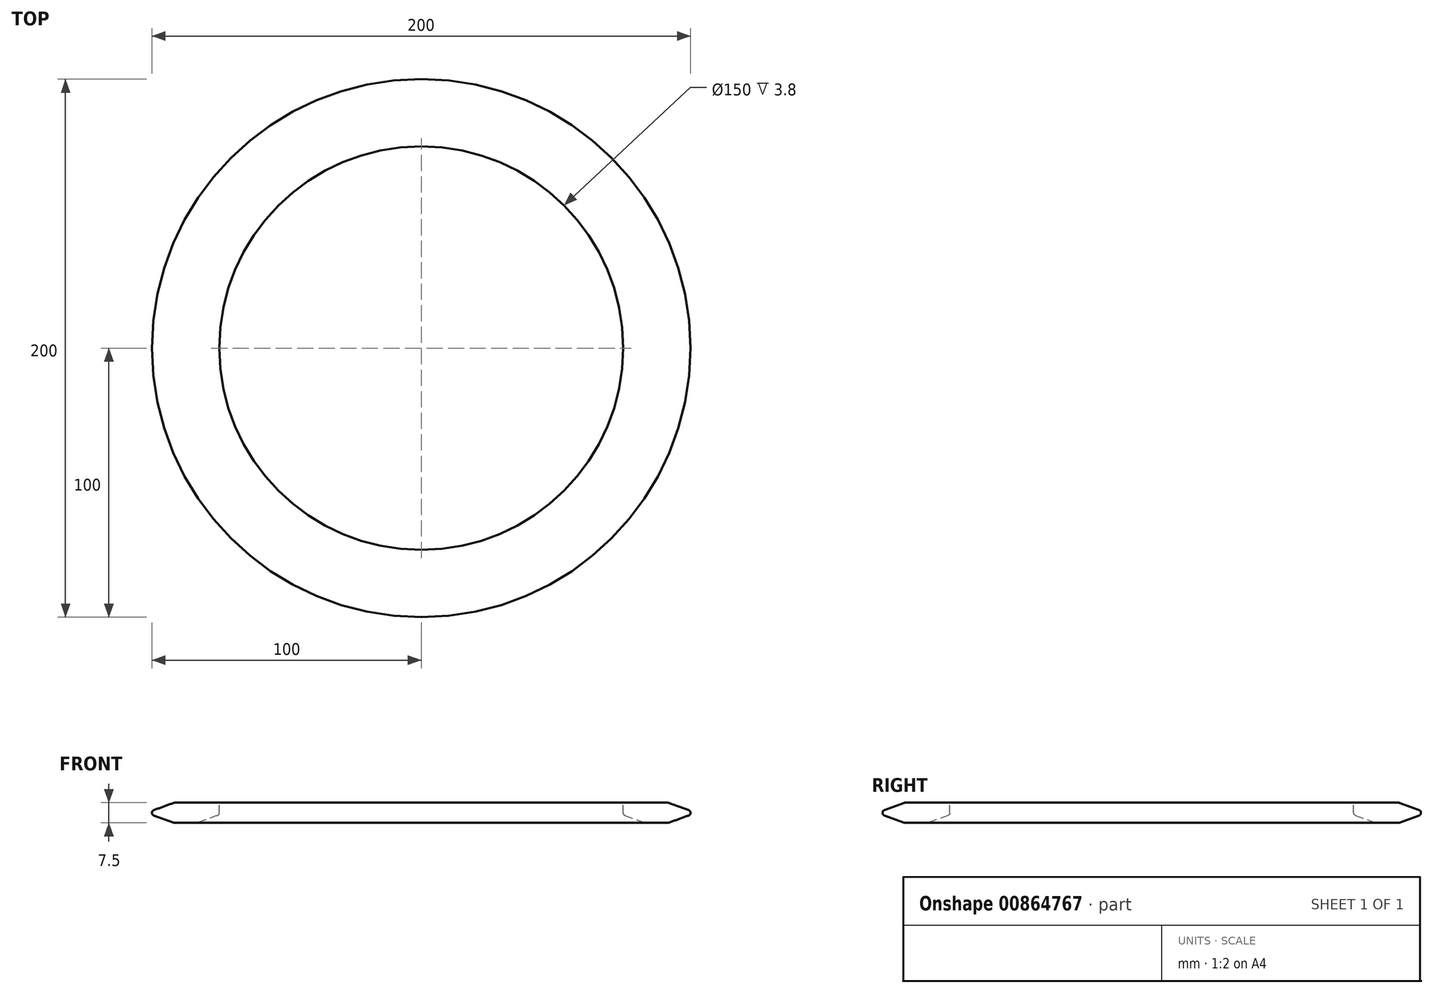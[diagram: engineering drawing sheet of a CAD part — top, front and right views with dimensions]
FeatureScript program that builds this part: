
annotation { "Feature Type Name" : "Feature", "Feature Type Description" : "" }
export const myFeature = defineFeature(function(context is Context, id is Id, definition is map)
    precondition{}
    {
        {
            var Q0;
            Q0=qCreatedBy(makeId("Top.planeOp"),FACE);
            var sketch = newSketch(context, id + "F0", { "sketchPlane" : qUnion([Q0])});
            skCircle(sketch, "E0", {"center": v(0, 0) * mm, "radius": 100 * mm});
            skSolve(sketch);
        }
        {
            var Q0;
            Q0=makeQuery(id+"F0.imprint","IMPRINT",FACE,{"disambiguationData":[TD([[makeQuery(id+"F0.imprint","IMPRINT",EDGE,{"derivedFrom":sQuery(id+"F0.wireOp",EDGE,"E0")}),1.0]])]});
            extrude(context, id + "F1", {"entities" : qUnion([Q0]), "depth" : 7.5 * mm, "offsetDistance" : 25 * mm});
        }
        {
            var Q0;
            Q0=makeQuery(id+"F1.opExtrude","CAP_FACE",FACE,{"disambiguationData":[OSD([sQuery(id+"F0.wireOp",EDGE,"E0")])],"isStart":false});
            var sketch = newSketch(context, id + "F2", { "sketchPlane" : qUnion([Q0])});
            skCircle(sketch, "E1", {"center": v(0, 0) * mm, "radius": 75 * mm});
            skSolve(sketch);
        }
        {
            var Q0;
            Q0=qSketchRegion(id+"F2",true);
            extrude(context, id + "F3", {"entities" : qUnion([Q0]), "operationType" : NewBodyOperationType.REMOVE, "oppositeDirection" : true, "depth" : 25 * mm, "offsetDistance" : 25 * mm});
        }
        {
            var Q0;
            Q0=makeQuery(id+"F1.opExtrude","CAP_EDGE",EDGE,{"disambiguationData":[OSD([sQuery(id+"F0.wireOp",EDGE,"E0")])],"isStart":true});
            var Q1;
            Q1=makeQuery(id+"F1.opExtrude","CAP_EDGE",EDGE,{"disambiguationData":[OSD([sQuery(id+"F0.wireOp",EDGE,"E0")])],"isStart":false});
            var Q2;
            Q2=makeQuery(id+"F3.boolean.opBoolean","INTERSECT",EDGE,{"derivedFrom":[makeQuery(id+"F1.opExtrude","CAP_FACE",FACE,{"disambiguationData":[OSD([sQuery(id+"F0.wireOp",EDGE,"E0")])],"isStart":true}),makeQuery(id+"F3.opExtrude","SWEPT_FACE",FACE,{"disambiguationData":[OSD([sQuery(id+"F2.wireOp",EDGE,"E1")])]})]});
            var Q3;
            Q3=makeQuery(id+"F3.boolean.opBoolean","COPY",EDGE,{"derivedFrom":makeQuery(id+"F3.opExtrude","CAP_EDGE",EDGE,{"disambiguationData":[OSD([sQuery(id+"F2.wireOp",EDGE,"E1")])],"isStart":true})});
            chamfer(context, id + "F4", {"entities" : qUnion([Q0, Q1, Q2, Q3]), "chamferType" : ChamferType.OFFSET_ANGLE, "width" : 3 * mm, "oppositeDirection" : false, "angle" : 70 * degree, "tangentPropagation" : true});
        }
        {
            var Q0;
            {var subQ0=sQuery(id+"F0.wireOp",EDGE,"E0");Q0=makeQuery(id+"F4.opChamfer","BLEND_EDGE",EDGE,{"blendedFrom":[makeQuery(id+"F1.opExtrude","CAP_EDGE",EDGE,{"disambiguationData":[OSD([subQ0])],"isStart":true}),makeQuery(id+"F1.opExtrude","SWEPT_FACE",FACE,{"disambiguationData":[OSD([subQ0])]})],"blendedInto":[makeQuery(id+"F1.opExtrude","SWEPT_FACE",FACE,{"disambiguationData":[OSD([subQ0])]})]});}
            var Q1;
            {var subQ0=sQuery(id+"F0.wireOp",EDGE,"E0");Q1=makeQuery(id+"F4.opChamfer","BLEND_EDGE",EDGE,{"blendedFrom":[makeQuery(id+"F1.opExtrude","CAP_EDGE",EDGE,{"disambiguationData":[OSD([subQ0])],"isStart":false}),makeQuery(id+"F1.opExtrude","SWEPT_FACE",FACE,{"disambiguationData":[OSD([subQ0])]})],"blendedInto":[makeQuery(id+"F1.opExtrude","SWEPT_FACE",FACE,{"disambiguationData":[OSD([subQ0])]})]});}
            var Q2;
            {var subQ0=sQuery(id+"F0.wireOp",EDGE,"E0");Q2=makeQuery(id+"F4.opChamfer","BLEND_EDGE",EDGE,{"blendedFrom":[makeQuery(id+"F1.opExtrude","CAP_EDGE",EDGE,{"disambiguationData":[OSD([subQ0])],"isStart":true}),makeQuery(id+"F1.opExtrude","CAP_FACE",FACE,{"disambiguationData":[OSD([subQ0])],"isStart":true})],"blendedInto":[makeQuery(id+"F1.opExtrude","CAP_FACE",FACE,{"disambiguationData":[OSD([subQ0])],"isStart":true})]});}
            var Q3;
            {var subQ0=makeQuery(id+"F1.opExtrude","CAP_FACE",FACE,{"disambiguationData":[OSD([sQuery(id+"F0.wireOp",EDGE,"E0")])],"isStart":true});Q3=makeQuery(id+"F4.opChamfer","BLEND_EDGE",EDGE,{"blendedFrom":[makeQuery(id+"F3.boolean.opBoolean","INTERSECT",EDGE,{"derivedFrom":[subQ0,makeQuery(id+"F3.opExtrude","SWEPT_FACE",FACE,{"disambiguationData":[OSD([sQuery(id+"F2.wireOp",EDGE,"E1")])]})]}),subQ0],"blendedInto":[subQ0]});}
            var Q4;
            {var subQ0=makeQuery(id+"F3.opExtrude","SWEPT_FACE",FACE,{"disambiguationData":[OSD([sQuery(id+"F2.wireOp",EDGE,"E1")])]});Q4=makeQuery(id+"F4.opChamfer","BLEND_EDGE",EDGE,{"blendedFrom":[makeQuery(id+"F3.boolean.opBoolean","INTERSECT",EDGE,{"derivedFrom":[makeQuery(id+"F1.opExtrude","CAP_FACE",FACE,{"disambiguationData":[OSD([sQuery(id+"F0.wireOp",EDGE,"E0")])],"isStart":true}),subQ0]}),makeQuery(id+"F3.boolean.opBoolean","COPY",FACE,{"derivedFrom":subQ0})],"blendedInto":[makeQuery(id+"F3.boolean.opBoolean","COPY",FACE,{"derivedFrom":subQ0})]});}
            var Q5;
            {var subQ0=sQuery(id+"F2.wireOp",EDGE,"E1");Q5=makeQuery(id+"F4.opChamfer","BLEND_EDGE",EDGE,{"blendedFrom":[makeQuery(id+"F3.boolean.opBoolean","COPY",EDGE,{"derivedFrom":makeQuery(id+"F3.opExtrude","CAP_EDGE",EDGE,{"disambiguationData":[OSD([subQ0])],"isStart":true})}),makeQuery(id+"F3.boolean.opBoolean","COPY",FACE,{"derivedFrom":makeQuery(id+"F3.opExtrude","SWEPT_FACE",FACE,{"disambiguationData":[OSD([subQ0])]})})],"blendedInto":[makeQuery(id+"F3.boolean.opBoolean","COPY",FACE,{"derivedFrom":makeQuery(id+"F3.opExtrude","SWEPT_FACE",FACE,{"disambiguationData":[OSD([subQ0])]})})]});}
            var Q6;
            {var subQ0=sQuery(id+"F0.wireOp",EDGE,"E0");Q6=makeQuery(id+"F4.opChamfer","BLEND_EDGE",EDGE,{"blendedFrom":[makeQuery(id+"F1.opExtrude","CAP_EDGE",EDGE,{"disambiguationData":[OSD([subQ0])],"isStart":false}),makeQuery(id+"F1.opExtrude","CAP_FACE",FACE,{"disambiguationData":[OSD([subQ0])],"isStart":false})],"blendedInto":[makeQuery(id+"F1.opExtrude","CAP_FACE",FACE,{"disambiguationData":[OSD([subQ0])],"isStart":false})]});}
            var Q7;
            Q7=makeQuery(id+"F4.opChamfer","BLEND_EDGE",EDGE,{"blendedFrom":[makeQuery(id+"F3.boolean.opBoolean","COPY",EDGE,{"derivedFrom":makeQuery(id+"F3.opExtrude","CAP_EDGE",EDGE,{"disambiguationData":[OSD([sQuery(id+"F2.wireOp",EDGE,"E1")])],"isStart":true})}),makeQuery(id+"F1.opExtrude","CAP_FACE",FACE,{"disambiguationData":[OSD([sQuery(id+"F0.wireOp",EDGE,"E0")])],"isStart":false})],"blendedInto":[makeQuery(id+"F1.opExtrude","CAP_FACE",FACE,{"disambiguationData":[OSD([sQuery(id+"F0.wireOp",EDGE,"E0")])],"isStart":false})]});
            fillet(context, id + "F5", {"entities" : qUnion([Q0, Q1, Q2, Q3, Q4, Q5, Q6, Q7]), "radius" : 1 * mm, "tangentPropagation" : true, "allowEdgeOverflow" : false});
        }
    });
